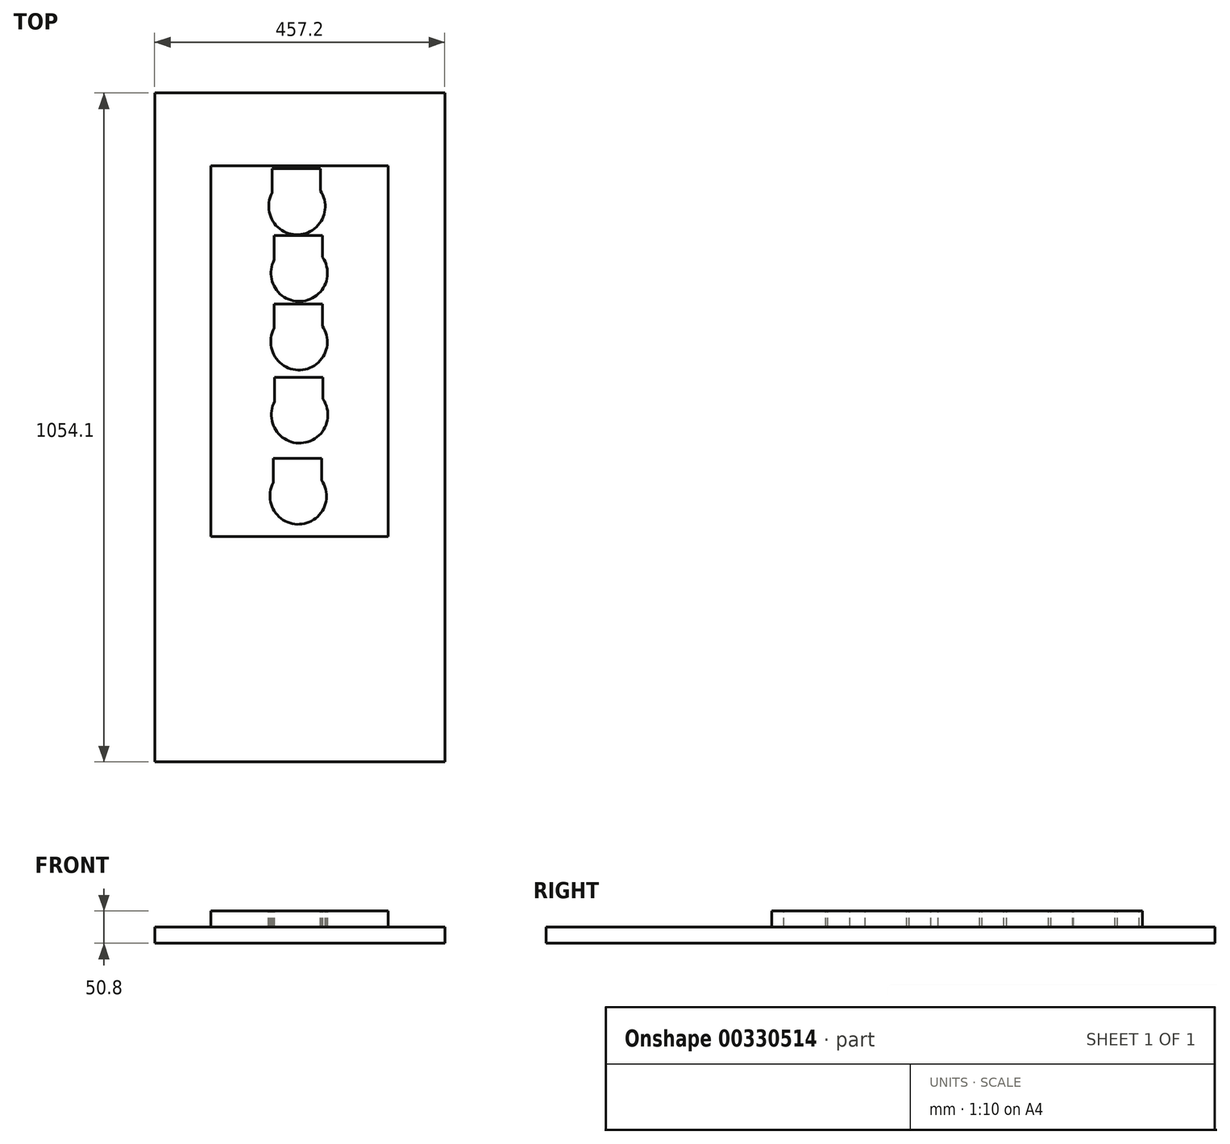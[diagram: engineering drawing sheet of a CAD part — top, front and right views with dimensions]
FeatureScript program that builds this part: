
annotation { "Feature Type Name" : "Feature", "Feature Type Description" : "" }
export const myFeature = defineFeature(function(context is Context, id is Id, definition is map)
    precondition{}
    {
        {
            var Q0;
            Q0=qCreatedBy(makeId("Top.planeOp"),FACE);
            var sketch = newSketch(context, id + "F0", { "sketchPlane" : qUnion([Q0])});
            skLineSegment(sketch, "E0.bottom", {"start": v(-273.88, 631.52) * mm, "end": v(183.32, 631.52) * mm});
            skLineSegment(sketch, "E0.top", {"start": v(-273.88, -422.58) * mm, "end": v(183.32, -422.58) * mm});
            skLineSegment(sketch, "E0.left", {"start": v(-273.88, 631.52) * mm, "end": v(-273.88, -422.58) * mm});
            skLineSegment(sketch, "E0.right", {"start": v(183.32, 631.52) * mm, "end": v(183.32, -422.58) * mm});
            skSolve(sketch);
        }
        {
            var Q0;
            Q0 = qSketchRegion(id + "F0", true);
            extrude(context, id + "F1", {"entities" : qUnion([Q0]), "depth" : 25.4 * mm});
        }
        {
            var Q0;
            {var subQ0=sQuery(id+"F0.wireOp",EDGE,"E0.left");var subQ2=sQuery(id+"F0.wireOp",EDGE,"E0.top");var subQ3=sQuery(id+"F0.wireOp",EDGE,"E0.right");var subQ5=sQuery(id+"F0.wireOp",EDGE,"E0.bottom");Q0=makeQuery(id+"FYKCDpLrNTEqoV5_1.boolean.opBoolean","SPLIT",FACE,{"disambiguationData":[TD([makeQuery(id+"F1.opExtrude","SWEPT_FACE",FACE,{"disambiguationData":[OSD([subQ2])]})])],"derivedFrom":makeQuery(id+"F1.opExtrude","CAP_FACE",FACE,{"disambiguationData":[OSD([subQ5,subQ2,subQ0,subQ3])],"isStart":false})});}
            var sketch = newSketch(context, id + "F2", { "sketchPlane" : qUnion([Q0])});
            skLineSegment(sketch, "E1.bottom", {"start": v(-185.58, 516.67) * mm, "end": v(93.82, 516.67) * mm});
            skLineSegment(sketch, "E1.top", {"start": v(-185.58, -67.53) * mm, "end": v(93.82, -67.53) * mm});
            skLineSegment(sketch, "E1.left", {"start": v(-185.58, 516.67) * mm, "end": v(-185.58, -67.53) * mm});
            skLineSegment(sketch, "E1.right", {"start": v(93.82, 516.67) * mm, "end": v(93.82, -67.53) * mm});
            skSolve(sketch);
        }
        {
            var Q0;
            Q0 = qSketchRegion(id + "F2", true);
            extrude(context, id + "F3", {"entities" : qUnion([Q0]), "operationType" : NewBodyOperationType.ADD, "depth" : 25.4 * mm});
        }
        {
            var Q0;
            Q0=makeQuery(id+"F3.opExtrude","CAP_FACE",FACE,{"disambiguationData":[OSD([sQuery(id+"F2.wireOp",EDGE,"E1.bottom"),sQuery(id+"F2.wireOp",EDGE,"E1.top"),sQuery(id+"F2.wireOp",EDGE,"E1.left"),sQuery(id+"F2.wireOp",EDGE,"E1.right")])],"isStart":false});
            var sketch = newSketch(context, id + "F4", { "sketchPlane" : qUnion([Q0])});
            skArc(sketch, "E2", {"start": v(-86.84, 17.63) * mm, "mid": v(-45.48, -48.07) * mm, "end": v(-10.64, 21.3) * mm});
            skLineSegment(sketch, "E3", {"start": v(-86.84, 17.63) * mm, "end": v(-86.84, 55.73) * mm});
            skLineSegment(sketch, "E4", {"start": v(-86.84, 55.73) * mm, "end": v(-10.64, 55.73) * mm});
            skLineSegment(sketch, "E5", {"start": v(-10.64, 55.73) * mm, "end": v(-10.64, 21.3) * mm});
            skArc(sketch, "E6", {"start": v(-84.69, 145.56) * mm, "mid": v(-43.34, 79.87) * mm, "end": v(-8.49, 149.23) * mm});
            skLineSegment(sketch, "E7", {"start": v(-84.69, 145.56) * mm, "end": v(-84.69, 183.66) * mm});
            skLineSegment(sketch, "E8", {"start": v(-84.69, 183.66) * mm, "end": v(-8.49, 183.66) * mm});
            skLineSegment(sketch, "E9", {"start": v(-8.49, 183.66) * mm, "end": v(-8.49, 149.23) * mm});
            skArc(sketch, "E10", {"start": v(-85.56, 260.66) * mm, "mid": v(-44.2, 194.96) * mm, "end": v(-9.36, 264.33) * mm});
            skLineSegment(sketch, "E11", {"start": v(-85.56, 260.66) * mm, "end": v(-85.56, 298.76) * mm});
            skLineSegment(sketch, "E12", {"start": v(-85.56, 298.76) * mm, "end": v(-9.36, 298.76) * mm});
            skLineSegment(sketch, "E13", {"start": v(-9.36, 298.76) * mm, "end": v(-9.36, 264.33) * mm});
            skArc(sketch, "E14", {"start": v(-85.3, 368.87) * mm, "mid": v(-43.95, 303.18) * mm, "end": v(-9.1, 372.54) * mm});
            skLineSegment(sketch, "E15", {"start": v(-85.3, 368.87) * mm, "end": v(-85.3, 406.97) * mm});
            skLineSegment(sketch, "E16", {"start": v(-85.3, 406.97) * mm, "end": v(-9.1, 406.97) * mm});
            skLineSegment(sketch, "E17", {"start": v(-9.1, 406.97) * mm, "end": v(-9.1, 372.54) * mm});
            skArc(sketch, "E18", {"start": v(-88.83, 473.96) * mm, "mid": v(-47.47, 408.26) * mm, "end": v(-12.63, 477.63) * mm});
            skLineSegment(sketch, "E19", {"start": v(-88.83, 473.96) * mm, "end": v(-88.83, 512.06) * mm});
            skLineSegment(sketch, "E20", {"start": v(-88.83, 512.06) * mm, "end": v(-12.63, 512.06) * mm});
            skLineSegment(sketch, "E21", {"start": v(-12.63, 512.06) * mm, "end": v(-12.63, 477.63) * mm});
            skSolve(sketch);
        }
        {
            var Q0;
            Q0 = qSketchRegion(id + "F4", true);
            extrude(context, id + "F5", {"entities" : qUnion([Q0]), "operationType" : NewBodyOperationType.REMOVE, "oppositeDirection" : true, "depth" : 25.4 * mm});
        }
    });
